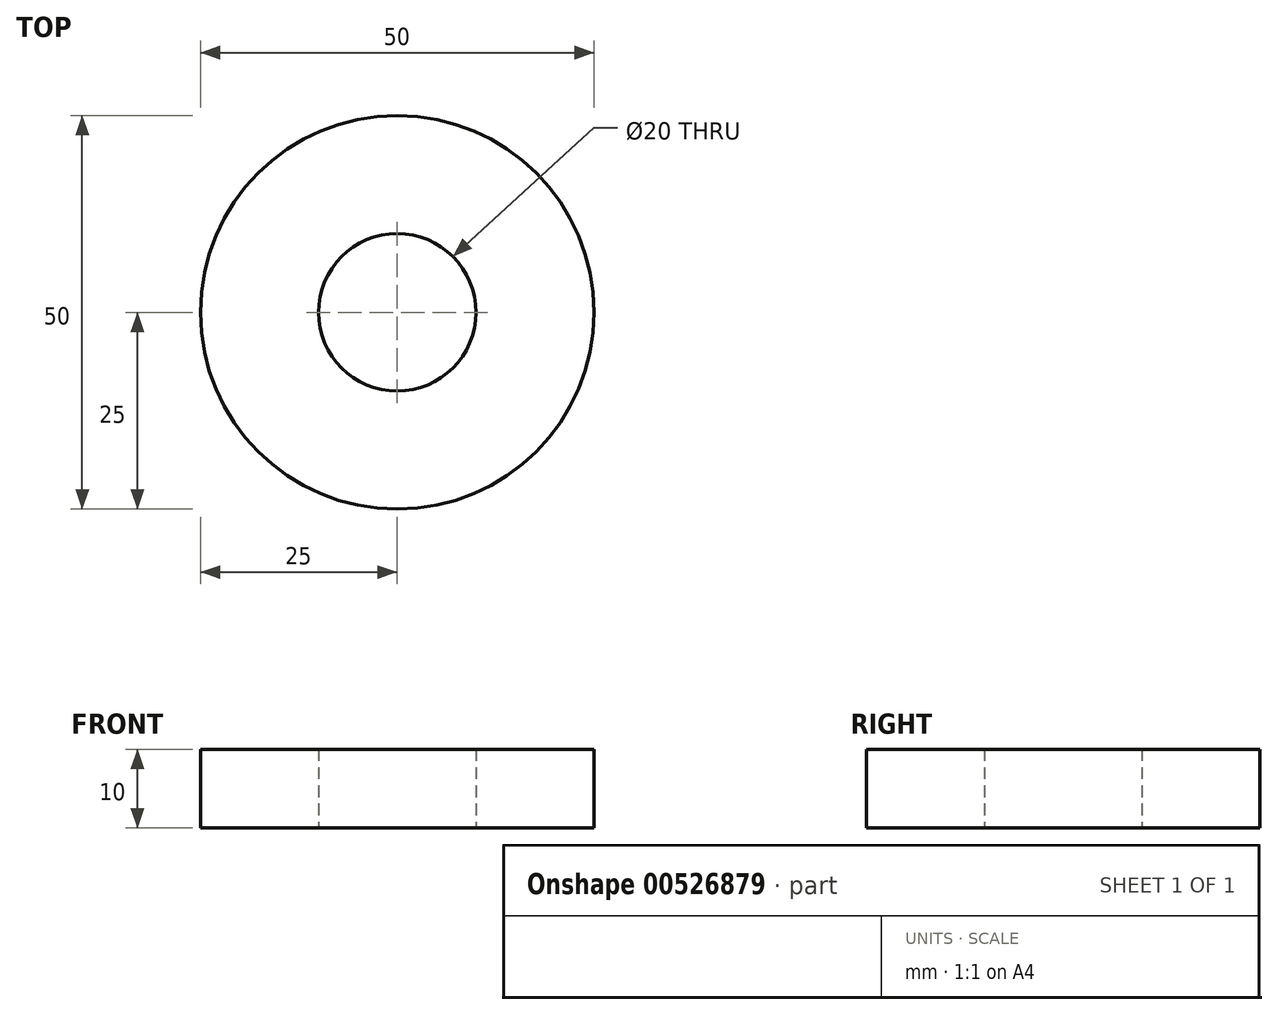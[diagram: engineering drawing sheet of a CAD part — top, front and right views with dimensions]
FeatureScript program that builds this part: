
annotation { "Feature Type Name" : "Feature", "Feature Type Description" : "" }
export const myFeature = defineFeature(function(context is Context, id is Id, definition is map)
    precondition{}
    {
        {
            var Q0;
            Q0=qCreatedBy(makeId("Top.planeOp"),FACE);
            var sketch = newSketch(context, id + "F0", { "sketchPlane" : qUnion([Q0])});
            skCircle(sketch, "E0", {"center": v(0, 0) * mm, "radius": 25 * mm});
            skCircle(sketch, "E1", {"center": v(0, 0) * mm, "radius": 10 * mm});
            skSolve(sketch);
        }
        {
            var Q0;
            Q0 = qSketchRegion(id + "F0", true);
            extrude(context, id + "F1", {"entities" : qUnion([Q0]), "endBound" : BoundingType.SYMMETRIC, "depth" : 10 * mm, "offsetDistance" : 25.4 * mm});
        }
    });
